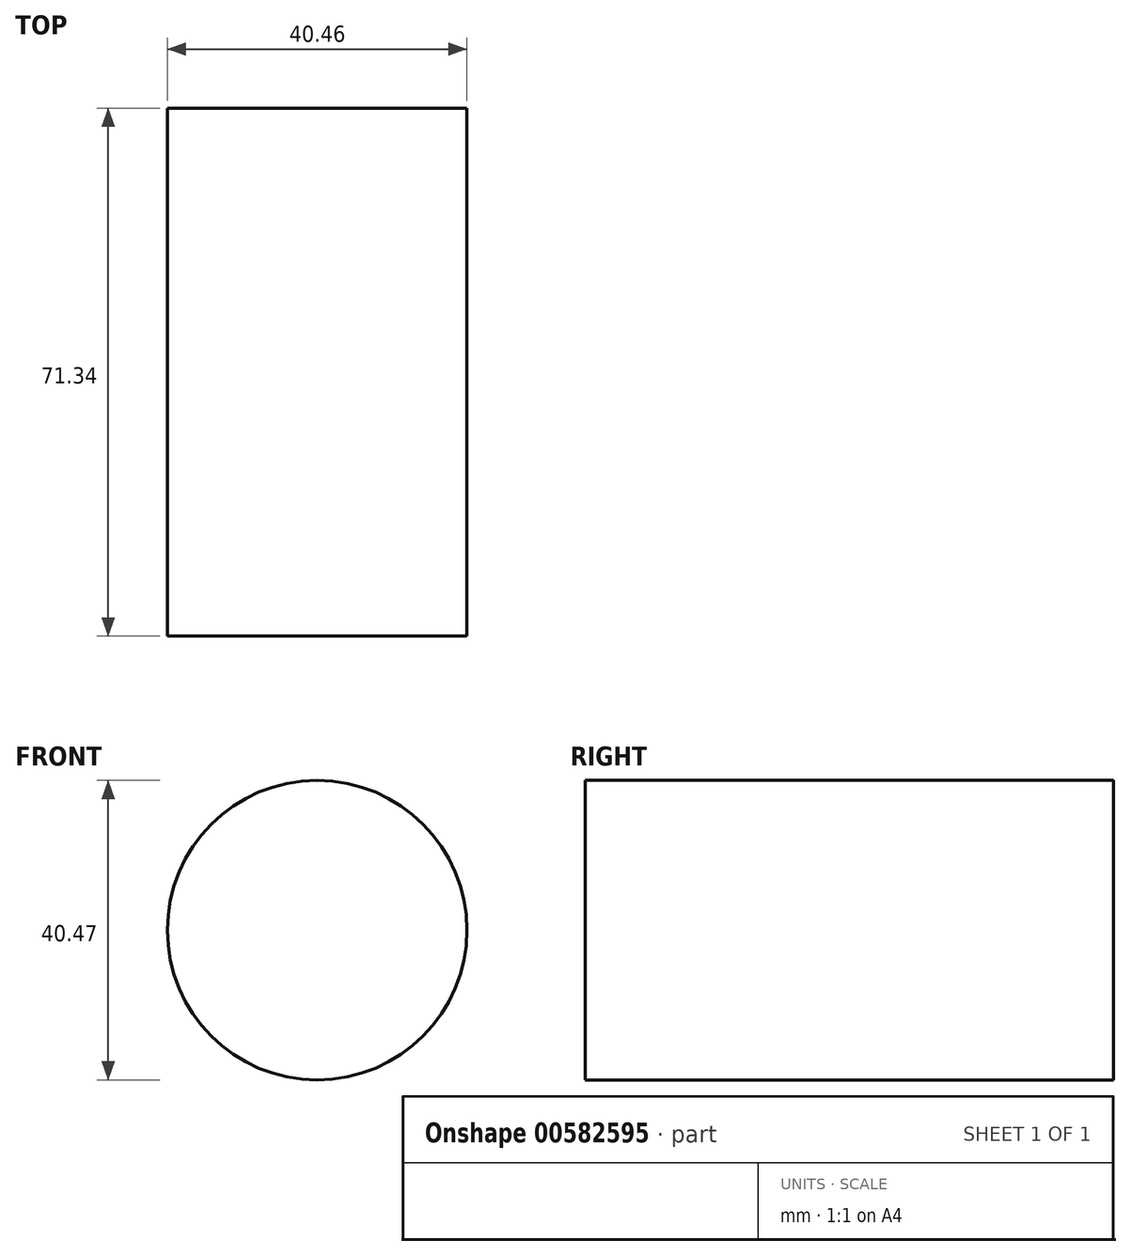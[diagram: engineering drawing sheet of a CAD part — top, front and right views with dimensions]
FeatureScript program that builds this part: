
annotation { "Feature Type Name" : "Feature", "Feature Type Description" : "" }
export const myFeature = defineFeature(function(context is Context, id is Id, definition is map)
    precondition{}
    {
        {
            var Q0;
            Q0=qCreatedBy(makeId("Front.planeOp"),FACE);
            var sketch = newSketch(context, id + "F0", { "sketchPlane" : qUnion([Q0])});
            skCircle(sketch, "E0", {"center": v(6.5, 40.2) * mm, "radius": 20.23 * mm});
            skSolve(sketch);
        }
        {
            var Q0;
            Q0=makeQuery(id+"F0.imprint","IMPRINT",FACE,{"disambiguationData":[TD([[makeQuery(id+"F0.imprint","IMPRINT",EDGE,{"derivedFrom":sQuery(id+"F0.wireOp",EDGE,"E0")}),1.0]])]});
            extrude(context, id + "F1", {"entities" : qUnion([Q0]), "depth" : 71.34 * mm, "offsetDistance" : 25.4 * mm});
        }
    });
